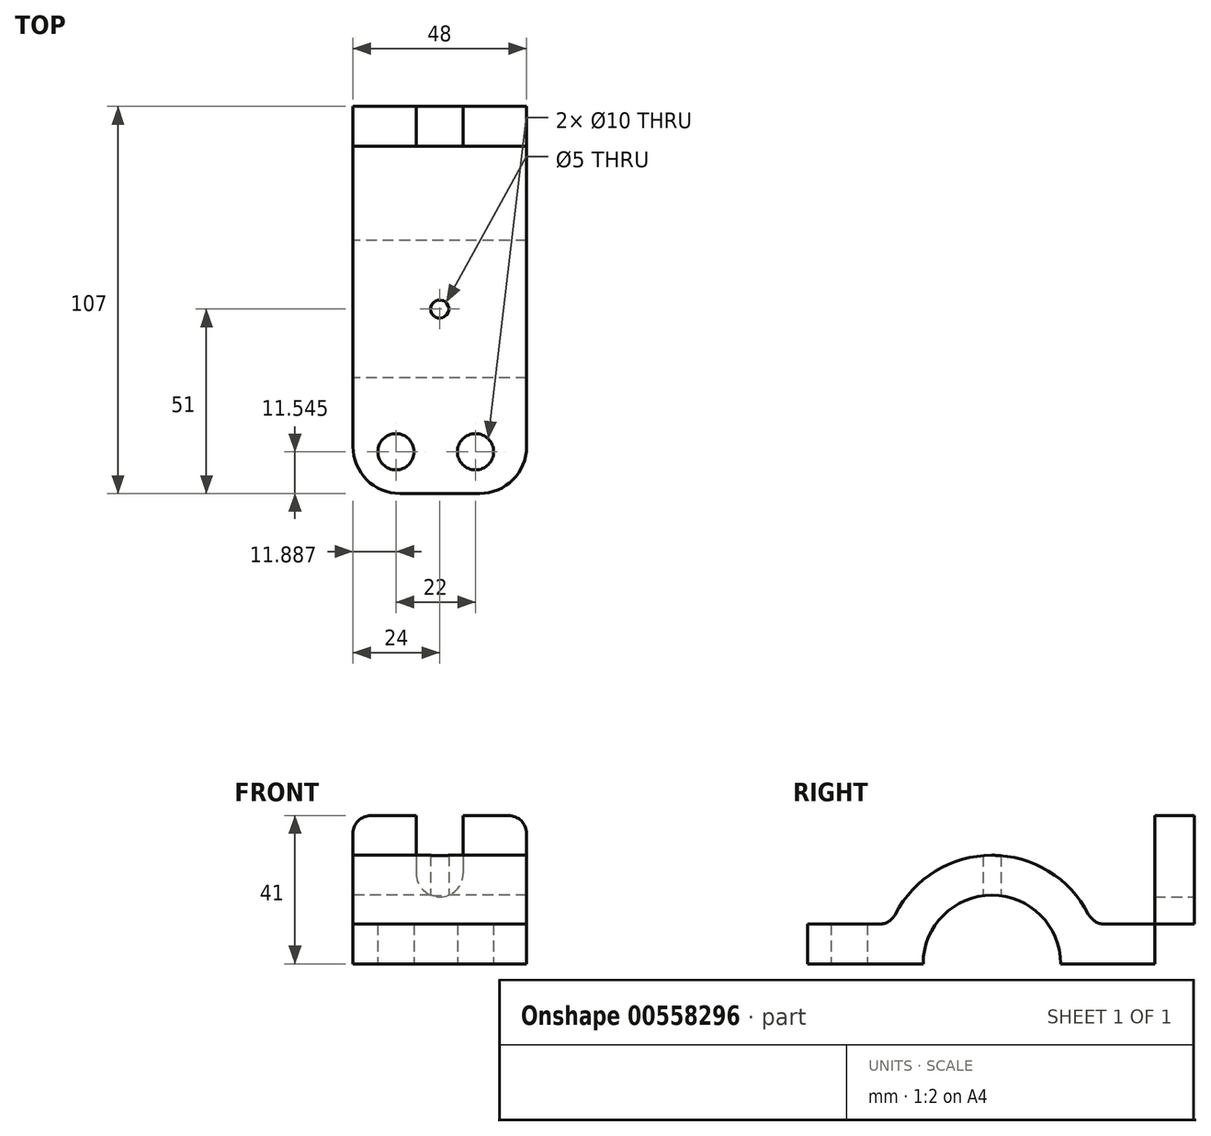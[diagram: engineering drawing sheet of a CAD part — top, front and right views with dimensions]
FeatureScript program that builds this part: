
annotation { "Feature Type Name" : "Feature", "Feature Type Description" : "" }
export const myFeature = defineFeature(function(context is Context, id is Id, definition is map)
    precondition{}
    {
        {
            var Q0;
            Q0=qCreatedBy(makeId("Right.planeOp"),FACE);
            var sketch = newSketch(context, id + "F0", { "sketchPlane" : qUnion([Q0])});
            skCircle(sketch, "E0", {"center": v(0, 0) * mm, "radius": 30 * mm});
            skCircle(sketch, "E1", {"center": v(0, 0) * mm, "radius": 19 * mm});
            skLineSegment(sketch, "E2.bottom", {"start": v(-51, 0) * mm, "end": v(56, 0) * mm});
            skLineSegment(sketch, "E2.top", {"start": v(-51, 11) * mm, "end": v(56, 11) * mm});
            skLineSegment(sketch, "E2.left", {"start": v(-51, 0) * mm, "end": v(-51, 11) * mm});
            skLineSegment(sketch, "E2.right", {"start": v(56, 0) * mm, "end": v(56, 11) * mm});
            skLineSegment(sketch, "E3.bottom", {"start": v(56, 0) * mm, "end": v(45, 0) * mm});
            skLineSegment(sketch, "E3.top", {"start": v(56, 41) * mm, "end": v(45, 41) * mm});
            skLineSegment(sketch, "E3.left", {"start": v(56, 0) * mm, "end": v(56, 41) * mm});
            skLineSegment(sketch, "E3.right", {"start": v(45, 0) * mm, "end": v(45, 41) * mm});
            skSolve(sketch);
        }
        {
            var Q0;
            {var subQ5=sQuery(id+"F0.wireOp",EDGE,"E2.left");Q0=makeQuery(id+"F0.imprint","IMPRINT",FACE,{"disambiguationData":[TD([[makeQuery(id+"F0.imprint","IMPRINT",EDGE,{"derivedFrom":subQ5}),-1.0]])]});}
            var Q1;
            {var subQ0=sQuery(id+"F0.wireOp",EDGE,"E2.top");var subQ1=sQuery(id+"F0.wireOp",EDGE,"E0");var subQ2=makeQuery(id+"F0.imprint","INTERSECT",VERTEX,{"disambiguationData":[OD(1.0)],"derivedFrom":[subQ1,subQ0]});Q1=makeQuery(id+"F0.imprint","IMPRINT",FACE,{"disambiguationData":[TD([[makeQuery(id+"F0.imprint","IMPRINT",EDGE,{"disambiguationData":[TD([[subQ2,-1.0]])],"derivedFrom":subQ1}),1.0]])]});}
            var Q2;
            {var subQ0=sQuery(id+"F0.wireOp",EDGE,"E2.top");var subQ1=sQuery(id+"F0.wireOp",EDGE,"E0");var subQ2=makeQuery(id+"F0.imprint","INTERSECT",VERTEX,{"disambiguationData":[OD(0.0)],"derivedFrom":[subQ1,subQ0]});Q2=makeQuery(id+"F0.imprint","IMPRINT",FACE,{"disambiguationData":[TD([[makeQuery(id+"F0.imprint","IMPRINT",EDGE,{"disambiguationData":[TD([[subQ2,-1.0]])],"derivedFrom":subQ1}),1.0]])]});}
            var Q3;
            {var subQ0=sQuery(id+"F0.wireOp",EDGE,"E2.top");var subQ1=sQuery(id+"F0.wireOp",EDGE,"E0");var subQ2=makeQuery(id+"F0.imprint","INTERSECT",VERTEX,{"disambiguationData":[OD(0.0)],"derivedFrom":[subQ1,subQ0]});Q3=makeQuery(id+"F0.imprint","IMPRINT",FACE,{"disambiguationData":[TD([[makeQuery(id+"F0.imprint","IMPRINT",EDGE,{"disambiguationData":[TD([[subQ2,1.0]])],"derivedFrom":subQ1}),1.0]])]});}
            var Q4;
            {var subQ0=sQuery(id+"F0.wireOp",EDGE,"E2.top");var subQ1=sQuery(id+"F0.wireOp",EDGE,"E0");var subQ2=makeQuery(id+"F0.imprint","INTERSECT",VERTEX,{"disambiguationData":[OD(0.0)],"derivedFrom":[subQ1,subQ0]});Q4=makeQuery(id+"F0.imprint","IMPRINT",FACE,{"disambiguationData":[TD([[makeQuery(id+"F0.imprint","IMPRINT",EDGE,{"disambiguationData":[TD([[subQ2,1.0]])],"derivedFrom":subQ1}),-1.0]])]});}
            var Q5;
            {var subQ5=sQuery(id+"F0.wireOp",EDGE,"E3.bottom");Q5=makeQuery(id+"F0.imprint","IMPRINT",FACE,{"disambiguationData":[TD([[makeQuery(id+"F0.imprint","IMPRINT",EDGE,{"derivedFrom":subQ5}),-1.0]])]});}
            var Q6;
            {var subQ5=sQuery(id+"F0.wireOp",EDGE,"E3.top");Q6=makeQuery(id+"F0.imprint","IMPRINT",FACE,{"disambiguationData":[TD([[makeQuery(id+"F0.imprint","IMPRINT",EDGE,{"derivedFrom":subQ5}),1.0]])]});}
            extrude(context, id + "F1", {"entities" : qUnion([Q0, Q1, Q2, Q3, Q4, Q5, Q6]), "endBound" : BoundingType.SYMMETRIC, "depth" : 48 * mm, "offsetDistance" : 25 * mm});
        }
        {
            var Q0;
            Q0=makeQuery(id+"F1.opExtrude","SWEPT_FACE",FACE,{"disambiguationData":[OSD([sQuery(id+"F0.wireOp",EDGE,"E3.left")])]});
            var sketch = newSketch(context, id + "F2", { "sketchPlane" : qUnion([Q0])});
            skLineSegment(sketch, "E4", {"start": v(0, 0) * mm, "end": v(0, 41) * mm, "construction": true});
            skCircle(sketch, "E5", {"center": v(0, 25) * mm, "radius": 6.5 * mm});
            skLineSegment(sketch, "E6", {"start": v(6.5, 25) * mm, "end": v(6.5, 41) * mm});
            skLineSegment(sketch, "E7", {"start": v(-6.5, 25) * mm, "end": v(-6.5, 41) * mm});
            skSolve(sketch);
        }
        {
            var Q0;
            Q0 = qSketchRegion(id + "F2", true);
            var Q1;
            {var subQ0=sQuery(id+"F2.wireOp",EDGE,"E6");Q1=makeQuery(id+"F2.imprint","IMPRINT",FACE,{"disambiguationData":[TD([[makeQuery(id+"F2.imprint","IMPRINT",EDGE,{"derivedFrom":subQ0}),1.0]])]});}
            extrude(context, id + "F3", {"entities" : qUnion([Q0, Q1]), "operationType" : NewBodyOperationType.REMOVE, "endBound" : BoundingType.SYMMETRIC, "oppositeDirection" : true, "depth" : 25 * mm, "offsetDistance" : 25 * mm});
        }
        {
            var Q0;
            Q0=qCreatedBy(makeId("Top.planeOp"),FACE);
            var sketch = newSketch(context, id + "F4", { "sketchPlane" : qUnion([Q0])});
            skCircle(sketch, "E8", {"center": v(0, 0) * mm, "radius": 2.5 * mm});
            skLineSegment(sketch, "E9", {"start": v(-24, -39.46) * mm, "end": v(24, -39.46) * mm, "construction": true});
            skLineSegment(sketch, "E10", {"start": v(0, -51) * mm, "end": v(0, -27.91) * mm, "construction": true});
            skCircle(sketch, "E11", {"center": v(-12.11, -39.46) * mm, "radius": 5 * mm});
            skCircle(sketch, "E12", {"center": v(9.89, -39.46) * mm, "radius": 5 * mm});
            skSolve(sketch);
        }
        {
            var Q0;
            Q0 = qSketchRegion(id + "F4", true);
            extrude(context, id + "F5", {"entities" : qUnion([Q0]), "operationType" : NewBodyOperationType.REMOVE, "endBound" : BoundingType.SYMMETRIC, "depth" : 112 * mm, "offsetDistance" : 25 * mm});
        }
        {
            var Q0;
            Q0=makeQuery(id+"F1.opExtrude","CAP_EDGE",EDGE,{"disambiguationData":[OSD([sQuery(id+"F0.wireOp",EDGE,"E2.left")])],"isStart":true});
            var Q1;
            Q1=makeQuery(id+"F1.opExtrude","CAP_EDGE",EDGE,{"disambiguationData":[OSD([sQuery(id+"F0.wireOp",EDGE,"E2.left")])],"isStart":false});
            fillet(context, id + "F6", {"entities" : qUnion([Q0, Q1]), "radius" : 13 * mm, "tangentPropagation" : true, "allowEdgeOverflow" : false});
        }
        {
            var Q0;
            Q0=makeQuery(id+"F1.opExtrude","CAP_EDGE",EDGE,{"disambiguationData":[OSD([sQuery(id+"F0.wireOp",EDGE,"E3.top")])],"isStart":true});
            var Q1;
            Q1=makeQuery(id+"F1.opExtrude","CAP_EDGE",EDGE,{"disambiguationData":[OSD([sQuery(id+"F0.wireOp",EDGE,"E3.top")])],"isStart":false});
            fillet(context, id + "F7", {"entities" : qUnion([Q0, Q1]), "radius" : 5 * mm, "tangentPropagation" : true, "allowEdgeOverflow" : false});
        }
        {
            var Q0;
            {var subQ0=sQuery(id+"F0.wireOp",EDGE,"E2.top");var subQ1=sQuery(id+"F0.wireOp",EDGE,"E0");Q0=makeQuery(id+"F1.opExtrude","SWEPT_EDGE",EDGE,{"disambiguationData":[OSD([subQ1,subQ0]),TDD([makeQuery(id+"F0.imprint","INTERSECT",VERTEX,{"disambiguationData":[OD(0.0)],"derivedFrom":[subQ1,subQ0]})])]});}
            var Q1;
            {var subQ0=sQuery(id+"F0.wireOp",EDGE,"E2.top");var subQ1=sQuery(id+"F0.wireOp",EDGE,"E0");Q1=makeQuery(id+"F1.opExtrude","SWEPT_EDGE",EDGE,{"disambiguationData":[OSD([subQ1,subQ0]),TDD([makeQuery(id+"F0.imprint","INTERSECT",VERTEX,{"disambiguationData":[OD(1.0)],"derivedFrom":[subQ1,subQ0]})])]});}
            fillet(context, id + "F8", {"entities" : qUnion([Q0, Q1]), "radius" : 5 * mm, "tangentPropagation" : true, "allowEdgeOverflow" : false});
        }
    });
